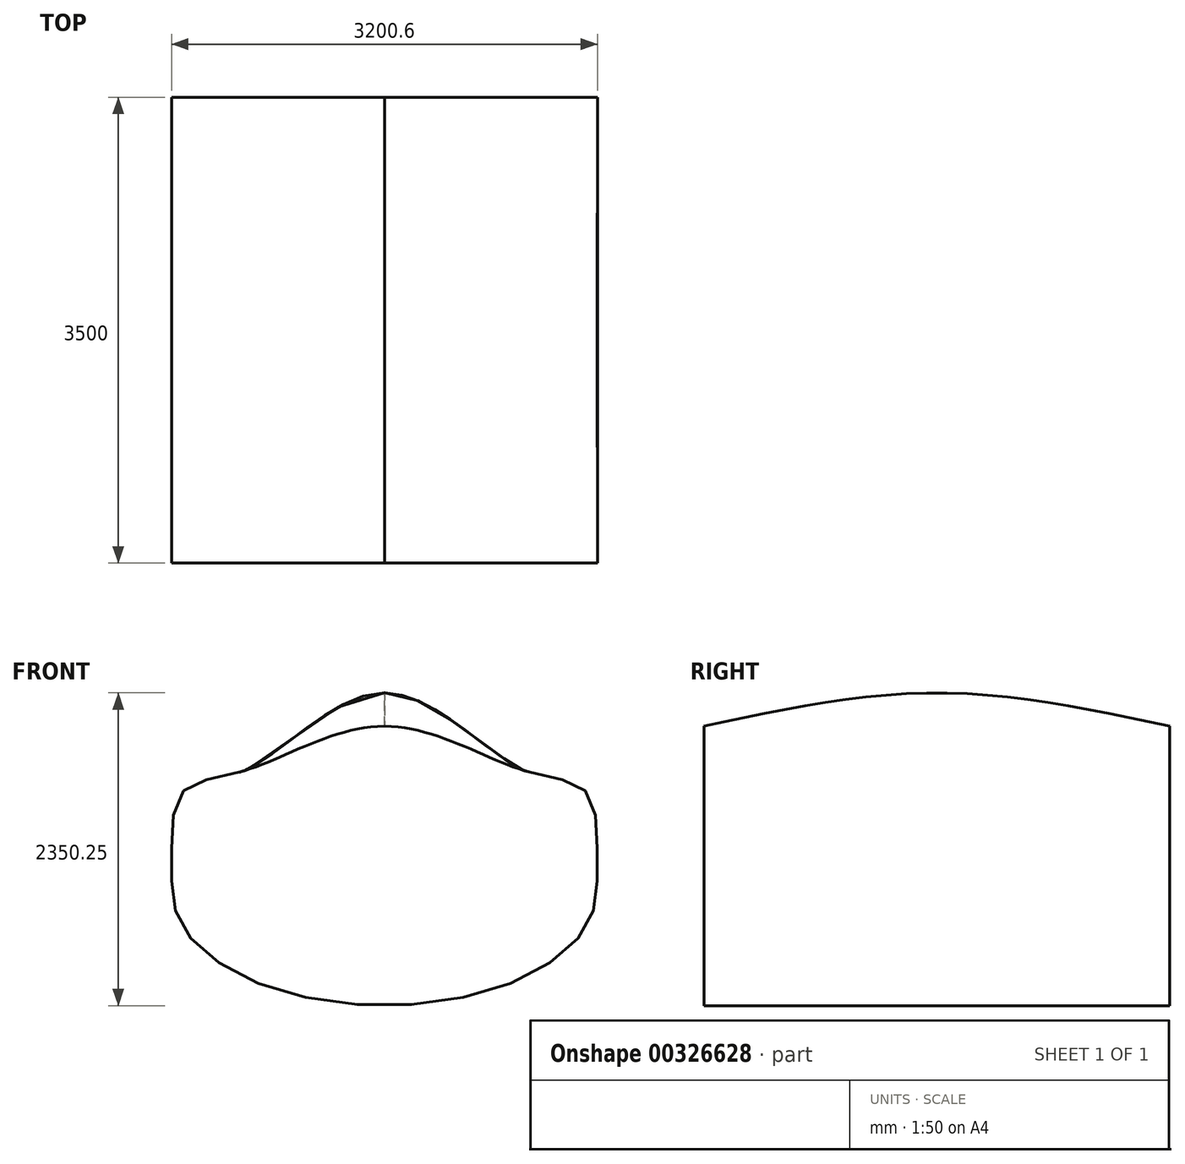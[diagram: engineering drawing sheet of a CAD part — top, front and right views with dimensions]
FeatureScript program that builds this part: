
annotation { "Feature Type Name" : "Feature", "Feature Type Description" : "" }
export const myFeature = defineFeature(function(context is Context, id is Id, definition is map)
    precondition{}
    {
        {
            var Q0;
            Q0=qCreatedBy(makeId("Front.planeOp"),FACE);
            cPlane(context, id + "F0", {"entities" : qUnion([Q0]), "cplaneType" : CPlaneType.OFFSET, "offset" : 3500 * mm, "width" : 150 * mm, "height" : 150 * mm});
        }
        {
            var Q0;
            Q0=qCreatedBy(id+"F0.planeOp",FACE);
            var sketch = newSketch(context, id + "F1", { "sketchPlane" : qUnion([Q0])});
            skPoint(sketch, "E0.middle", {"position": v(0, 0) * mm});
            skFitSpline(sketch, "E1", {"points": [v(0, 1000) * mm, v(1060, 662.5) * mm, v(1517.6, 506.84) * mm, v(1600, 0) * mm, v(1517.6, -506.84) * mm, v(750, -1000) * mm, v(-750, -1000) * mm, v(-1517.6, -506.84) * mm, v(-1600, 0) * mm, v(-1517.6, 506.84) * mm, v(-1060, 662.5) * mm, v(0, 1000) * mm]});
            skSolve(sketch);
        }
        {
            var Q0;
            Q0=qCreatedBy(makeId("Front.planeOp"),FACE);
            var sketch = newSketch(context, id + "F2", { "sketchPlane" : qUnion([Q0])});
            skPoint(sketch, "E2.middle", {"position": v(0, 0) * mm});
            skFitSpline(sketch, "E3", {"points": [v(0, 1000) * mm, v(1060, 662.5) * mm, v(1517.6, 506.84) * mm, v(1600, 0) * mm, v(1517.6, -506.84) * mm, v(750, -1000) * mm, v(-750, -1000) * mm, v(-1517.6, -506.84) * mm, v(-1600, 0) * mm, v(-1517.6, 506.84) * mm, v(-1060, 662.5) * mm, v(0, 1000) * mm]});
            skSolve(sketch);
        }
        {
            var Q0;
            Q0=qCreatedBy(makeId("Front.planeOp"),FACE);
            cPlane(context, id + "F3", {"entities" : qUnion([Q0]), "cplaneType" : CPlaneType.OFFSET, "offset" : 1750 * mm, "width" : 150 * mm, "height" : 150 * mm});
        }
        {
            var Q0;
            Q0=qCreatedBy(id+"F3.planeOp",FACE);
            var sketch = newSketch(context, id + "F4", { "sketchPlane" : qUnion([Q0])});
            skPoint(sketch, "E4.middle", {"position": v(0, 0) * mm});
            skFitSpline(sketch, "E5", {"points": [v(0, 1250) * mm, v(1060, 662.5) * mm, v(1517.6, 506.84) * mm, v(1600, 0) * mm, v(1517.6, -506.84) * mm, v(750, -1000) * mm, v(-750, -1000) * mm, v(-1517.6, -506.84) * mm, v(-1600, 0) * mm, v(-1517.6, 506.84) * mm, v(-1060, 662.5) * mm, v(0, 1250) * mm]});
            skSolve(sketch);
        }
        {
            var Q0;
            Q0=makeQuery(id+"F1.imprint","IMPRINT",FACE,{"disambiguationData":[TD([[makeQuery(id+"F1.imprint","IMPRINT",EDGE,{"derivedFrom":sQuery(id+"F1.wireOp",EDGE,"E1")}),-1.0]])]});
            var Q1;
            Q1=makeQuery(id+"F4.imprint","IMPRINT",FACE,{"disambiguationData":[TD([[makeQuery(id+"F4.imprint","IMPRINT",EDGE,{"derivedFrom":sQuery(id+"F4.wireOp",EDGE,"E5")}),-1.0]])]});
            var Q2;
            Q2=makeQuery(id+"F2.imprint","IMPRINT",FACE,{"disambiguationData":[TD([[makeQuery(id+"F2.imprint","IMPRINT",EDGE,{"derivedFrom":sQuery(id+"F2.wireOp",EDGE,"E3")}),-1.0]])]});
            loft(context, id + "F5", {"sheetProfilesArray" : [{ "sheetProfileEntities" : qUnion([Q0]) }, { "sheetProfileEntities" : qUnion([Q1]) }, { "sheetProfileEntities" : qUnion([Q2]) }]});
        }
    });
